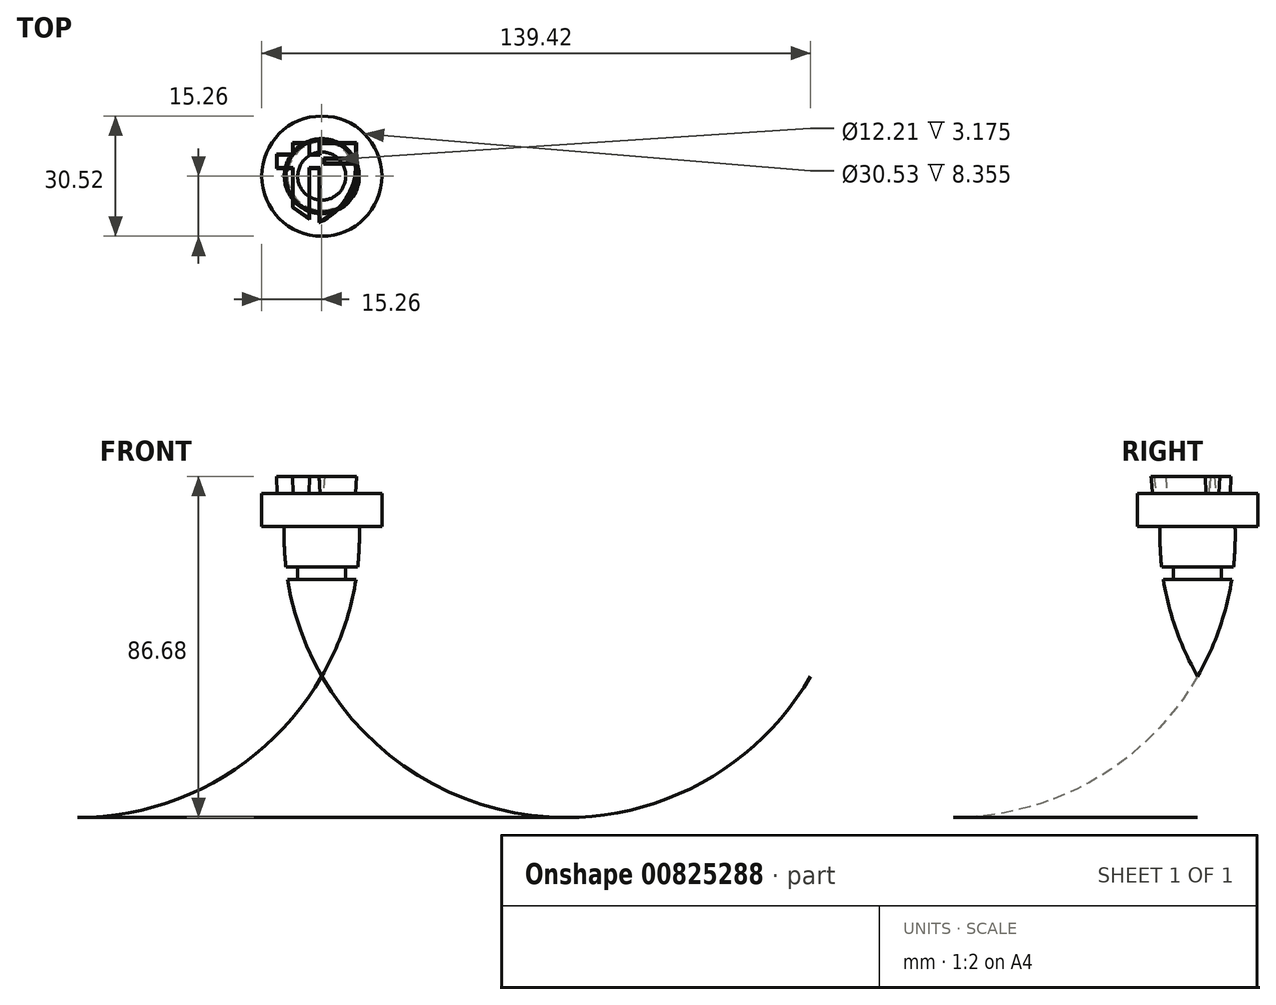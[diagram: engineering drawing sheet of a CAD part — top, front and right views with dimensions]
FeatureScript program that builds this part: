
annotation { "Feature Type Name" : "Feature", "Feature Type Description" : "" }
export const myFeature = defineFeature(function(context is Context, id is Id, definition is map)
    precondition{}
    {
        {
            var Q0;
            Q0=qCreatedBy(makeId("Front.planeOp"),FACE);
            var sketch = newSketch(context, id + "F0", { "sketchPlane" : qUnion([Q0])});
            skLineSegment(sketch, "E0", {"start": v(0, 0) * mm, "end": v(0, -38.1) * mm});
            skArc(sketch, "E1", {"start": v(-9.53, 0) * mm, "mid": v(-9.5, -5.18) * mm, "end": v(-9.11, -10.35) * mm});
            skLineSegment(sketch, "E2", {"start": v(-9.53, 0) * mm, "end": v(-15.26, 0) * mm});
            skLineSegment(sketch, "E3", {"start": v(-15.26, 0) * mm, "end": v(-15.26, 8.36) * mm});
            skLineSegment(sketch, "E4", {"start": v(-15.26, 8.36) * mm, "end": v(0, 8.36) * mm});
            skLineSegment(sketch, "E5", {"start": v(0, 8.36) * mm, "end": v(0, 0) * mm});
            skLineSegment(sketch, "E6", {"start": v(-8.68, -13.53) * mm, "end": v(-6.1, -13.53) * mm});
            skLineSegment(sketch, "E7", {"start": v(-6.1, -13.53) * mm, "end": v(-6.1, -10.35) * mm});
            skLineSegment(sketch, "E8", {"start": v(-6.1, -10.35) * mm, "end": v(-9.11, -10.35) * mm});
            skArc(sketch, "E9.trimOffspring", {"start": v(-8.68, -13.53) * mm, "mid": v(-5.47, -26.21) * mm, "end": v(0, -38.1) * mm});
            skSolve(sketch);
        }
        {
            var Q0;
            Q0=makeQuery(id+"F0.imprint","IMPRINT",FACE,{"disambiguationData":[TD([[makeQuery(id+"F0.imprint","IMPRINT",EDGE,{"derivedFrom":sQuery(id+"F0.wireOp",EDGE,"E0")}),-1.0]])]});
            var Q1;
            Q1=sQuery(id+"F0.wireOp",EDGE,"E0");
            revolve(context, id + "F1", {"surfaceOperationType" : NewSurfaceOperationType.NEW, "entities" : qUnion([Q0]), "axis" : qUnion([Q1]), "revolveType" : RevolveType.FULL});
        }
        {
            var Q0;
            Q0=qCreatedBy(makeId("Top.planeOp"),FACE);
            var sketch = newSketch(context, id + "F2", { "sketchPlane" : qUnion([Q0])});
            skLineSegment(sketch, "E10", {"start": v(0, 2.6) * mm, "end": v(-3.71, 2.6) * mm});
            skLineSegment(sketch, "E11", {"start": v(-3.71, 4.97) * mm, "end": v(0, 4.97) * mm});
            skLineSegment(sketch, "E12", {"start": v(0, 4.97) * mm, "end": v(0, 2.6) * mm});
            skLineSegment(sketch, "E13", {"start": v(-3.71, 4.97) * mm, "end": v(-3.71, 7.83) * mm});
            skLineSegment(sketch, "E14", {"start": v(-3.71, 7.83) * mm, "end": v(-6.8, 7.83) * mm});
            skLineSegment(sketch, "E15", {"start": v(-6.8, 7.83) * mm, "end": v(-6.8, 4.97) * mm});
            skLineSegment(sketch, "E16", {"start": v(-6.8, 4.97) * mm, "end": v(-10.86, 4.97) * mm});
            skLineSegment(sketch, "E17", {"start": v(-10.86, 4.97) * mm, "end": v(-10.86, 2.6) * mm});
            skLineSegment(sketch, "E18", {"start": v(-10.86, 2.6) * mm, "end": v(-6.8, 2.6) * mm});
            skLineSegment(sketch, "E19", {"start": v(-6.8, 2.6) * mm, "end": v(-6.8, -7.65) * mm});
            skLineSegment(sketch, "E20", {"start": v(-6.8, -7.65) * mm, "end": v(-3.71, -9.79) * mm});
            skLineSegment(sketch, "E21", {"start": v(-3.71, -9.79) * mm, "end": v(-3.71, 2.6) * mm});
            skLineSegment(sketch, "E22", {"start": v(0, 4.97) * mm, "end": v(8.2, 4.97) * mm});
            skLineSegment(sketch, "E23", {"start": v(8.2, 4.97) * mm, "end": v(8.2, 7.83) * mm});
            skLineSegment(sketch, "E24", {"start": v(8.2, 7.83) * mm, "end": v(0, 7.83) * mm});
            skLineSegment(sketch, "E25", {"start": v(0, 7.83) * mm, "end": v(0, 4.97) * mm});
            skLineSegment(sketch, "E26", {"start": v(0, 2.6) * mm, "end": v(8.2, 2.6) * mm});
            skLineSegment(sketch, "E27", {"start": v(0, 2.6) * mm, "end": v(0, -10.74) * mm});
            skArc(sketch, "E28", {"start": v(0, -10.74) * mm, "mid": v(5.9, -5.18) * mm, "end": v(8.2, 2.6) * mm});
            skSolve(sketch);
        }
        {
            var Q0;
            Q0=makeQuery(id+"F2.imprint","IMPRINT",FACE,{"disambiguationData":[TD([[makeQuery(id+"F2.imprint","IMPRINT",EDGE,{"derivedFrom":sQuery(id+"F2.wireOp",EDGE,"E10")}),-1.0]])]});
            var Q1;
            Q1=makeQuery(id+"F2.imprint","IMPRINT",FACE,{"disambiguationData":[TD([[makeQuery(id+"F2.imprint","IMPRINT",EDGE,{"derivedFrom":sQuery(id+"F2.wireOp",EDGE,"E26")}),-1.0]])]});
            var Q2;
            Q2=makeQuery(id+"F2.imprint","IMPRINT",FACE,{"disambiguationData":[TD([[makeQuery(id+"F2.imprint","IMPRINT",EDGE,{"derivedFrom":sQuery(id+"F2.wireOp",EDGE,"E22")}),1.0]])]});
            extrude(context, id + "F3", {"entities" : qUnion([Q0, Q1, Q2]), "operationType" : NewBodyOperationType.ADD, "depth" : 12.7 * mm, "offsetDistance" : 25.4 * mm, "hasDraft" : true, "draftAngle" : 3 * degree});
        }
    });
